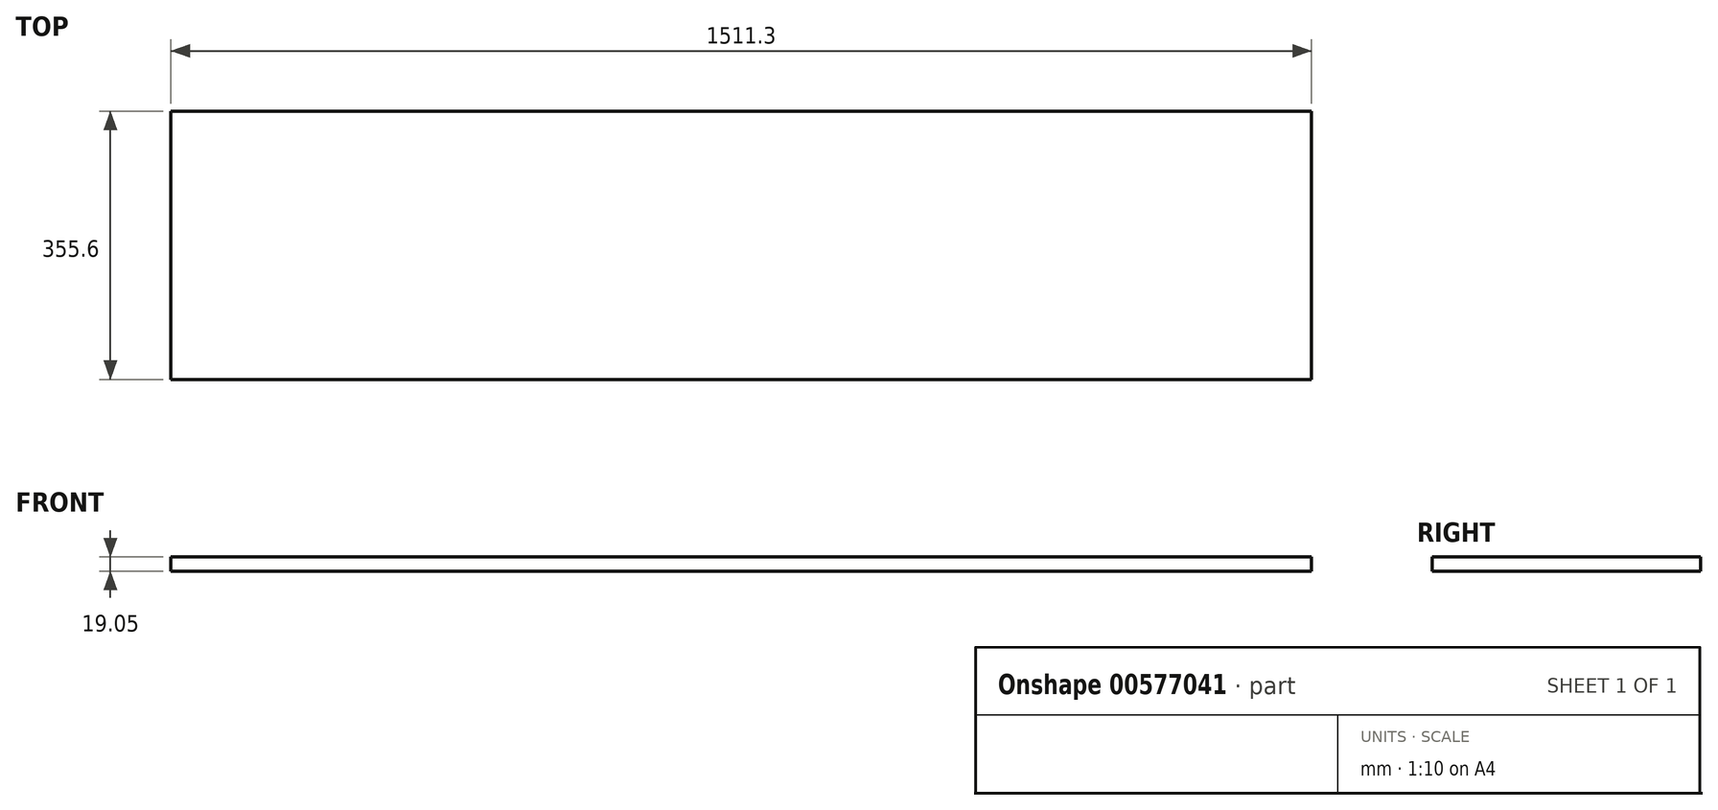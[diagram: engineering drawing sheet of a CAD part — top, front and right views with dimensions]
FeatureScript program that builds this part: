
annotation { "Feature Type Name" : "Feature", "Feature Type Description" : "" }
export const myFeature = defineFeature(function(context is Context, id is Id, definition is map)
    precondition{}
    {
        {
            var Q0;
            Q0=qCreatedBy(makeId("Top.planeOp"),FACE);
            var sketch = newSketch(context, id + "F0", { "sketchPlane" : qUnion([Q0])});
            skLineSegment(sketch, "E0.bottom", {"start": v(755.65, 177.8) * mm, "end": v(-755.65, 177.8) * mm});
            skLineSegment(sketch, "E0.top", {"start": v(755.65, -177.8) * mm, "end": v(-755.65, -177.8) * mm});
            skLineSegment(sketch, "E0.left", {"start": v(755.65, 177.8) * mm, "end": v(755.65, -177.8) * mm});
            skLineSegment(sketch, "E0.right", {"start": v(-755.65, 177.8) * mm, "end": v(-755.65, -177.8) * mm});
            skPoint(sketch, "E0.middle", {"position": v(0, 0) * mm});
            skSolve(sketch);
        }
        {
            var Q0;
            Q0=makeQuery(id+"F0.imprint","IMPRINT",FACE,{"disambiguationData":[TD([[makeQuery(id+"F0.imprint","IMPRINT",EDGE,{"derivedFrom":sQuery(id+"F0.wireOp",EDGE,"E0.bottom")}),1.0]])]});
            extrude(context, id + "F1", {"entities" : qUnion([Q0]), "depth" : 19.05 * mm, "offsetDistance" : 25.4 * mm});
        }
    });
